# Revit family: FOR UPDATE_72452XXX_NEWWWWW01
name_source: partatom
category: Plumbing Fixtures
revit_build: Autodesk Revit 2018 (Build: 20170223_1515(x64)
units: mm (PartAtom-declared; Revit-internal decimal feet)

## family parameters
Always vertical = No
Cut with Voids When Loaded = No
OmniClass Number = 23.45.55.17
OmniClass Title = Mixing Faucets
Part Type = Normal
Room Calculation Point = No
Round Connector Dimension = Use Diameter
Shared = No
Work Plane-Based = Yes

## types (1)
- 000 Chrome
    Always visible = Yes
    BIMobject category = Taps & Mixers
    Cold Water Inlet = 19 mm
    Cold Water Inlet Description = Cold Water Inlet 19.1 mm
    Default Elevation = 1219 mm
    Description = Rebris E Single lever bath mixer for exposed installation with centre distance 15.3 cm
    Design country = Germany
    EAN code = 4059625402054
    Edition number = 1
    GTIN code = https://4059625402054
    Hot Water Inlet = 19 mm
    Hot Water Inlet Description = Hot Water Inlet 19.1 mm
    IFC Classification = Valve
    Manufacturer = Hansgrohe
    Manufacturer country = Germany
    Manufacturer name = hansgrohe
    Material 1 = Hansgrohe - Metal - 000 Chrome
    Model = 72452XXX
    OmniClass Code = 23-31 11 00
    OmniClass Description = Faucets
    Product Guid = b305b3e5-cdcd-462c-96b1-e37022631c37
    Product SKU = 72452XXX
    Product data url = https://bimobject.com
    Product family = Rebris E
    Product group = Bath mixers
    Product name = 72452XXX Rebris E Single lever bath mixer for exposed installation with centre distance 15.3 cm
    QR code = https://bimobject.com
    UNSPSC Code = 301815
    URL = https://www.hansgrohe.com
    Weight Net (Kg) = 2

## geometry (parser evidence)
native form markers: Sweep x1
no freeform markers — native parametric forms only
